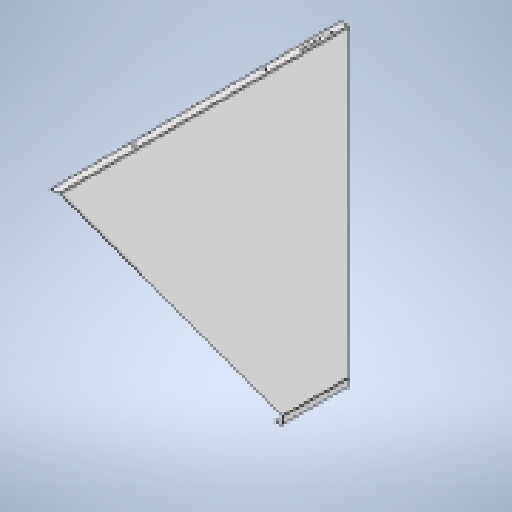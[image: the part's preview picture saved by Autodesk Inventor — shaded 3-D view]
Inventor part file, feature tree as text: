
AUTODESK INVENTOR PART (.ipt)
format: ipt  version: 2025.1 (Build 291241020, 241B)  size: 421,888 bytes
history: native  units: mm
features: sheet_metal_op x9, other x8, sketch x8, extrude x2, mirror x1, pattern_linear x1, projected_geometry x1
ambient origin geometry x8: Origin, YZ Plane, XZ Plane, XY Plane, X Axis, Y Axis, Z Axis, Center Point
bodies: Solid1 (feature_tree)
feature tree (30):
  sheet_metal_op  "Contour Flange1"
  extrude  "Extrusion6"  Depth=3.0mm
  other  "Mark2"
  other  "A-Side Definition"
  extrude  "Extrusion12"  Depth=6.0mm
  mirror  "Mirror1"
  sheet_metal_op  "Flange3"
  sheet_metal_op  "Flange4"
  pattern_linear  "Rectangular Pattern1"  Count1=174  [1 undecoded]
  sketch  "Sketch1"  dims[d6=3.0mm d7=3.0mm]
  other  "Plate1"
  sheet_metal_op  "Bend1"
  sheet_metal_op  "Corner1"
  sketch  "Sketch9"  dims[d8=1.5mm d9=6.0mm]
  sketch  "Sketch16"  dims[d10=5.0mm d11=1740.0mm]
  sketch  "Sketch17"  dims[d12=5.0mm]
  projected_geometry  "Projected Loop8"
  sketch  "Sketch18"  dims[d13=4.0mm]
  other  "Plate4"
  sheet_metal_op  "Bend4"
  sheet_metal_op  "Corner4"
  sketch  "Sketch19"  dims[d14=12.0mm]
  other  "Plate5"
  sheet_metal_op  "Bend5"
  sheet_metal_op  "Corner5"
  sketch  "Sketch20"  dims[d15=3.0mm]
  sketch  "Sketch21"  dims[d16=5.0mm d62=0.0mm d63=1170.0mm d64=8.0mm d68=10.0mm d69=0.0mm d93=400.0mm d97=3.0mm d98=120.0deg d99=8.0mm d100=0.0mm d101=175.0mm d103=850.499815mm d104=50.0mm d105=3.0mm d106=1.5mm d107=6.0mm d108=5.0mm d109=50.0mm d110=30.0deg d111=5.0mm d112=12.0mm d113=3.0mm d114=5.0mm d115=3.0mm d116=1.5mm d117=6.0mm d118=5.0mm d119=45.0mm d120=90.0deg d121=5.0mm d122=12.0mm d123=3.0mm d124=5.0mm d125=20.0mm d126=16.0mm d127=3.0mm d128=0.0mm d129=30.0mm d131=160.0mm d132=16.0mm d133=20.0mm d134=800.0mm d135=3.0mm d136=0.0mm]
  other  "Cut1"
  other  "Cut2"
  other  "Definition1"
note: 1 required parameter value undecoded (feature->parameter linkage not recoverable at this tier; creation-order binding heuristic only, values carry confidence <= 0.55)
